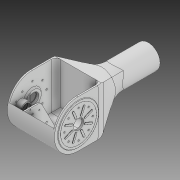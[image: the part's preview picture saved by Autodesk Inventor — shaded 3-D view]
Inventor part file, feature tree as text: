
AUTODESK INVENTOR PART (.ipt)
format: ipt  version: 2020 (Build 240168000, 168)  size: 877,568 bytes
history: native  units: mm
features: sketch x33, extrude x29, projected_geometry x8, plane x6, chamfer x3, fillet x3, pattern_circular x2, revolve x2, loft x2, other x2
ambient origin geometry x8: Origin, YZ Plane, XZ Plane, XY Plane, X Axis, Y Axis, Z Axis, Center Point
bodies: Solid1 (feature_tree)
feature tree (90):
  extrude  "Extrusion1"  Depth=250.0mm
  extrude  "Extrusion2"  Depth=100.0mm TaperAngle=0.0deg
  extrude  "Extrusion3"  TaperAngle=0.0deg  [1 undecoded]
  extrude  "Extrusion4"  Depth=10.0mm
  extrude  "Extrusion5"  Depth=30.0mm
  pattern_circular  "Circular Pattern1"  Count=8 Angle=360.0deg
  plane  "Work Plane1"
  plane  "Work Plane2"
  extrude  "Extrusion6"  Depth=30.0mm
  extrude  "Extrusion7"  Depth=2.0mm
  extrude  "Extrusion8"  Depth=2.0mm
  extrude  "Extrusion9"  [1 undecoded]
  chamfer  "Chamfer1"  Distance=10.0mm
  extrude  "Extrusion13"  Depth=10.0mm TaperAngle=0.0deg
  extrude  "Extrusion14"  Depth=5.0mm TaperAngle=0.0deg
  extrude  "Extrusion15"  Depth=95.1mm
  extrude  "Extrusion16"  Depth=10.0mm
  extrude  "Extrusion17"  Depth=80.0mm
  extrude  "Extrusion18"  Depth=60.0mm
  extrude  "Extrusion19"  Depth=80.0mm TaperAngle=360.0deg
  extrude  "Extrusion20"  Depth=15.5mm TaperAngle=0.0deg
  fillet  "Fillet2"  Radius=22.1mm
  pattern_circular  "Circular Pattern2"  Count=8 Angle=360.0deg
  extrude  "Extrusion22"  Depth=10.0mm
  plane  "Work Plane3"
  revolve  "Revolution1"  [1 undecoded]
  revolve  "Revolution2"  [1 undecoded]
  plane  "Work Plane4"
  extrude  "Extrusion23"  Depth=5.2mm
  extrude  "Extrusion24"  Depth=5.0mm
  fillet  "Fillet3"  Radius=5.2mm
  loft  "Loft1"
  extrude  "Extrusion25"  Depth=10.0mm
  extrude  "Extrusion26"  Depth=10.0mm
  extrude  "Extrusion27"  Depth=10.0mm
  extrude  "Extrusion28"  Depth=10.0mm
  plane  "Work Plane5"
  extrude  "Extrusion29"  Depth=10.0mm
  extrude  "Extrusion30"  Depth=10.0mm TaperAngle=0.0deg
  extrude  "Extrusion31"  Depth=10.0mm
  sketch  "Sketch38"  dims[d109=2.5mm d110=5.2mm]
  plane  "Work Plane6"
  extrude  "Extrusion33"  Depth=10.0mm TaperAngle=0.0deg
  loft  "Loft2"
  fillet  "Fillet5"  Radius=10.0mm
  chamfer  "Chamfer4"  Distance=18.8mm
  extrude  "Extrusion34"  Depth=10.0mm TaperAngle=0.0deg
  chamfer  "Chamfer5"  Distance=6.0mm
  sketch  "Sketch1"  dims[d0=50.0mm d1=250.0mm]
  sketch  "Sketch2"  dims[d2=50.0mm d3=100.0mm d4=0.0mm]
  sketch  "Sketch4"  dims[d5=5.0mm d7=0.0mm d8=0.0mm]
  sketch  "Sketch5"  dims[d11=10.0mm d12=0.0mm d14=85.0mm]
  sketch  "Sketch7"  dims[d15=1.0mm d16=0.0mm d17=30.0mm]
  projected_geometry  "Projected Loop1"
  sketch  "Sketch8"  dims[d18=3.3mm]
  projected_geometry  "Projected Loop2"
  projected_geometry  "Projected Loop4"
  sketch  "Sketch9"  dims[d19=15.0mm d20=0.0mm d21=80.0mm d22=360.0deg]
  sketch  "Sketch10"  dims[d24=30.0mm d25=30.0mm]
  sketch  "Sketch14"  dims[d30=-3.0mm d31=2.0mm]
  sketch  "Sketch15"  dims[d32=2.0mm d33=2.0mm]
  sketch  "Sketch16"  dims[d34=31.5mm d35=0.0mm d36=-5.0mm d38=10.0mm d39=0.0mm]
  sketch  "Sketch17"  dims[d40=22.1mm d41=10.0mm d42=0.0mm]
  sketch  "Sketch18"  dims[d43=5.0mm d44=3.0mm d45=0.0mm]
  sketch  "Sketch19"  dims[d56=3.0mm d57=2.0mm d58=45.0deg d62=95.1mm]
  sketch  "Sketch20"  dims[d63=10.0mm d64=0.0mm d65=3.0mm]
  sketch  "Sketch21"  dims[d66=0.5mm d67=0.0mm d68=80.0mm]
  sketch  "Sketch23"  dims[d69=15.5mm d70=0.0mm d71=60.0mm]
  other  "Work Axis1"
  sketch  "Sketch24"  dims[d72=3.2mm d73=80.0mm d75=360.0deg]
  sketch  "Sketch25"  dims[d77=15.5mm d78=0.0mm d79=15.5mm d80=0.0mm d81=22.1mm]
  projected_geometry  "Projected Loop5"
  projected_geometry  "Projected Loop6"
  sketch  "Sketch26"  dims[d82=0.0mm d83=0.0mm]
  sketch  "Sketch27"  dims[d84=76.0mm]
  sketch  "Sketch28"  dims[d85=0.1mm d86=0.0mm]
  sketch  "Sketch29"  dims[d87=15.0mm]
  sketch  "Sketch30"  dims[d88=2.0mm]
  sketch  "Sketch31"  dims[d89=22.5mm]
  sketch  "Sketch32"  dims[d90=0.8mm d91=0.0mm]
  sketch  "Sketch33"  dims[d92=0.2mm d93=80.0mm d94=360.0deg]
  projected_geometry  "Projected Loop7"
  sketch  "Sketch34"  dims[d96=24.43461mm d97=10.0mm]
  sketch  "Sketch35"  dims[d104=25.0mm d105=16.1mm]
  sketch  "Sketch36"  dims[d106=96.8mm d107=0.0mm d108=0.0mm]
  projected_geometry  "Projected Loop8"
  projected_geometry  "Projected Loop9"
  sketch  "Sketch39"  dims[d111=1.0mm d112=5.0mm d113=5.2mm]
  other  "Edges1"
  sketch  "Sketch40"  dims[d114=90.0deg d115=15.0mm d116=25.0mm d117=25.0mm d118=19.0mm d119=19.0mm d120=2.7mm d122=3.0mm d123=0.0mm d124=5.5mm d125=2.0mm d126=0.0mm d127=90.0deg d128=10.0mm d129=18.8mm d130=0.0mm d131=111.25mm d132=0.0mm d133=6.0mm d134=4.0mm d135=0.0mm d136=1.0mm d137=1.0mm d138=0.0mm d139=-7.0mm d140=1.0mm d141=1.0mm d142=0.0mm d143=7.0mm d144=5.0mm d145=6.0mm d146=0.0mm d147=90.0deg d148=0.0mm d149=90.0deg d150=0.0mm d151=0.0mm d152=27.0mm d153=0.0mm d154=4.712389mm d161=150.0mm d162=50.0mm d163=90.0mm d164=0.0mm d165=0.0mm d166=90.0deg d167=0.0mm d168=90.0deg d169=30.0mm d170=10.0mm d171=50.0mm d172=1.0mm d173=2.0mm d174=45.0deg d175=10.0mm d176=30.0mm d177=0.0mm d178=1.0mm d179=2.0mm d180=45.0deg d181=50.0mm d182=8.5mm]
note: 4 required parameter values undecoded (feature->parameter linkage not recoverable at this tier; creation-order binding heuristic only, values carry confidence <= 0.55)